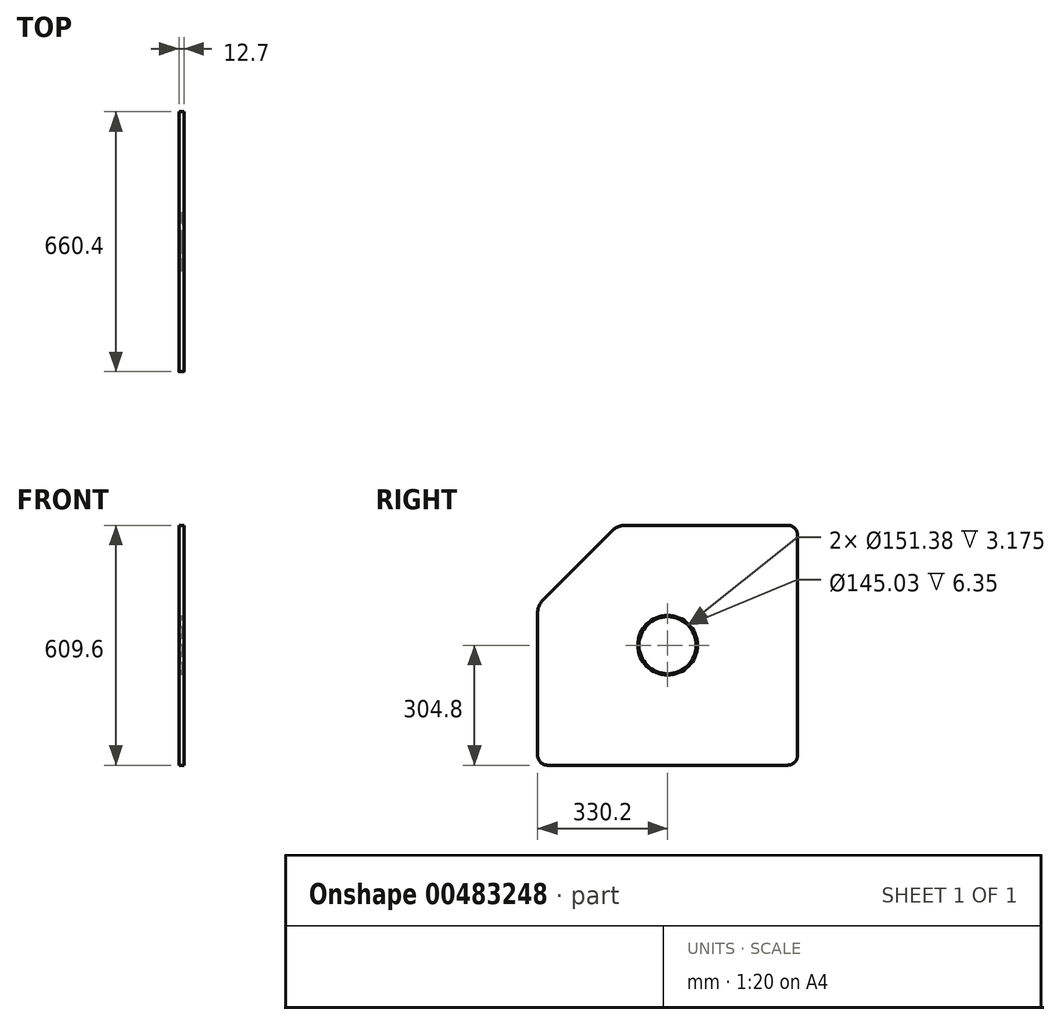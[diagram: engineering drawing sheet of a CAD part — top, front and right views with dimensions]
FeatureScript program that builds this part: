
annotation { "Feature Type Name" : "Feature", "Feature Type Description" : "" }
export const myFeature = defineFeature(function(context is Context, id is Id, definition is map)
    precondition{}
    {
        {
            var Q0;
            Q0=qCreatedBy(makeId("Right.planeOp"),FACE);
            var sketch = newSketch(context, id + "F0", { "sketchPlane" : qUnion([Q0])});
            skLineSegment(sketch, "E0.bottom", {"start": v(304.8, 304.8) * mm, "end": v(-105.96, 304.8) * mm});
            skLineSegment(sketch, "E0.top", {"start": v(304.8, -304.8) * mm, "end": v(-304.8, -304.8) * mm});
            skLineSegment(sketch, "E0.left", {"start": v(330.2, 279.4) * mm, "end": v(330.2, -279.4) * mm});
            skLineSegment(sketch, "E0.right", {"start": v(-330.2, 80.56) * mm, "end": v(-330.2, -279.4) * mm});
            skPoint(sketch, "E0.middle", {"position": v(0, 0) * mm});
            skLineSegment(sketch, "E1", {"start": v(-315.32, 116.48) * mm, "end": v(-141.88, 289.92) * mm});
            skPoint(sketch, "E2.orphan", {"position": v(-330.2, 304.8) * mm});
            skPoint(sketch, "E3.visualSharp", {"position": v(-127, 304.8) * mm});
            skArc(sketch, "E3.filletArc", {"start": v(-105.96, 304.8) * mm, "mid": v(-125.4, 300.93) * mm, "end": v(-141.88, 289.92) * mm});
            skPoint(sketch, "E4.visualSharp", {"position": v(-330.2, 101.6) * mm});
            skArc(sketch, "E4.filletArc", {"start": v(-315.32, 116.48) * mm, "mid": v(-326.33, 100) * mm, "end": v(-330.2, 80.56) * mm});
            skPoint(sketch, "E5.visualSharp", {"position": v(330.2, 304.8) * mm});
            skArc(sketch, "E5.filletArc", {"start": v(330.2, 279.4) * mm, "mid": v(322.76, 297.36) * mm, "end": v(304.8, 304.8) * mm});
            skPoint(sketch, "E6.visualSharp", {"position": v(-330.2, -304.8) * mm});
            skArc(sketch, "E6.filletArc", {"start": v(-330.2, -279.4) * mm, "mid": v(-322.76, -297.36) * mm, "end": v(-304.8, -304.8) * mm});
            skPoint(sketch, "E7.visualSharp", {"position": v(330.2, -304.8) * mm});
            skArc(sketch, "E7.filletArc", {"start": v(304.8, -304.8) * mm, "mid": v(322.76, -297.36) * mm, "end": v(330.2, -279.4) * mm});
            skSolve(sketch);
        }
        {
            var Q0;
            Q0 = qSketchRegion(id + "F0", true);
            extrude(context, id + "F1", {"entities" : qUnion([Q0]), "depth" : 12.7 * mm});
        }
        {
            var Q0;
            Q0=makeQuery(id+"F1.opExtrude","CAP_FACE",FACE,{"disambiguationData":[OSD([sQuery(id+"F0.wireOp",EDGE,"E0.bottom"),sQuery(id+"F0.wireOp",EDGE,"E0.top"),sQuery(id+"F0.wireOp",EDGE,"E0.left"),sQuery(id+"F0.wireOp",EDGE,"E0.right"),sQuery(id+"F0.wireOp",EDGE,"E1"),sQuery(id+"F0.wireOp",EDGE,"E3.filletArc"),sQuery(id+"F0.wireOp",EDGE,"E4.filletArc"),sQuery(id+"F0.wireOp",EDGE,"E5.filletArc"),sQuery(id+"F0.wireOp",EDGE,"E6.filletArc"),sQuery(id+"F0.wireOp",EDGE,"E7.filletArc")])],"isStart":false});
            var sketch = newSketch(context, id + "F2", { "sketchPlane" : qUnion([Q0])});
            skCircle(sketch, "E8", {"center": v(0, 0) * mm, "radius": 72.52 * mm});
            skSolve(sketch);
        }
        {
            var Q0;
            Q0 = qSketchRegion(id + "F2", true);
            extrude(context, id + "F3", {"entities" : qUnion([Q0]), "operationType" : NewBodyOperationType.REMOVE, "endBound" : BoundingType.THROUGH_ALL, "oppositeDirection" : true, "depth" : 25.4 * mm});
        }
        {
            var Q0;
            Q0=makeQuery(id+"F1.opExtrude","CAP_FACE",FACE,{"disambiguationData":[OSD([sQuery(id+"F0.wireOp",EDGE,"E0.bottom"),sQuery(id+"F0.wireOp",EDGE,"E0.top"),sQuery(id+"F0.wireOp",EDGE,"E0.left"),sQuery(id+"F0.wireOp",EDGE,"E0.right"),sQuery(id+"F0.wireOp",EDGE,"E1"),sQuery(id+"F0.wireOp",EDGE,"E3.filletArc"),sQuery(id+"F0.wireOp",EDGE,"E4.filletArc"),sQuery(id+"F0.wireOp",EDGE,"E5.filletArc"),sQuery(id+"F0.wireOp",EDGE,"E6.filletArc"),sQuery(id+"F0.wireOp",EDGE,"E7.filletArc")])],"isStart":false});
            var sketch = newSketch(context, id + "F4", { "sketchPlane" : qUnion([Q0])});
            skCircle(sketch, "E9.0", {"center": v(0, 0) * mm, "radius": 75.7 * mm});
            skSolve(sketch);
        }
        {
            var Q0;
            Q0 = qSketchRegion(id + "F4", true);
            extrude(context, id + "F5", {"entities" : qUnion([Q0]), "operationType" : NewBodyOperationType.REMOVE, "oppositeDirection" : true, "depth" : 3.17 * mm});
        }
        {
            var Q0;
            Q0=makeQuery(id+"F1.opExtrude","CAP_FACE",FACE,{"disambiguationData":[OSD([sQuery(id+"F0.wireOp",EDGE,"E0.bottom"),sQuery(id+"F0.wireOp",EDGE,"E0.top"),sQuery(id+"F0.wireOp",EDGE,"E0.left"),sQuery(id+"F0.wireOp",EDGE,"E0.right"),sQuery(id+"F0.wireOp",EDGE,"E1"),sQuery(id+"F0.wireOp",EDGE,"E3.filletArc"),sQuery(id+"F0.wireOp",EDGE,"E4.filletArc"),sQuery(id+"F0.wireOp",EDGE,"E5.filletArc"),sQuery(id+"F0.wireOp",EDGE,"E6.filletArc"),sQuery(id+"F0.wireOp",EDGE,"E7.filletArc")])],"isStart":true});
            var sketch = newSketch(context, id + "F6", { "sketchPlane" : qUnion([Q0])});
            skCircle(sketch, "E10.0", {"center": v(0, 0) * mm, "radius": 75.7 * mm});
            skSolve(sketch);
        }
        {
            var Q0;
            Q0 = qSketchRegion(id + "F6", true);
            extrude(context, id + "F7", {"entities" : qUnion([Q0]), "operationType" : NewBodyOperationType.REMOVE, "oppositeDirection" : true, "depth" : 3.17 * mm});
        }
    });
